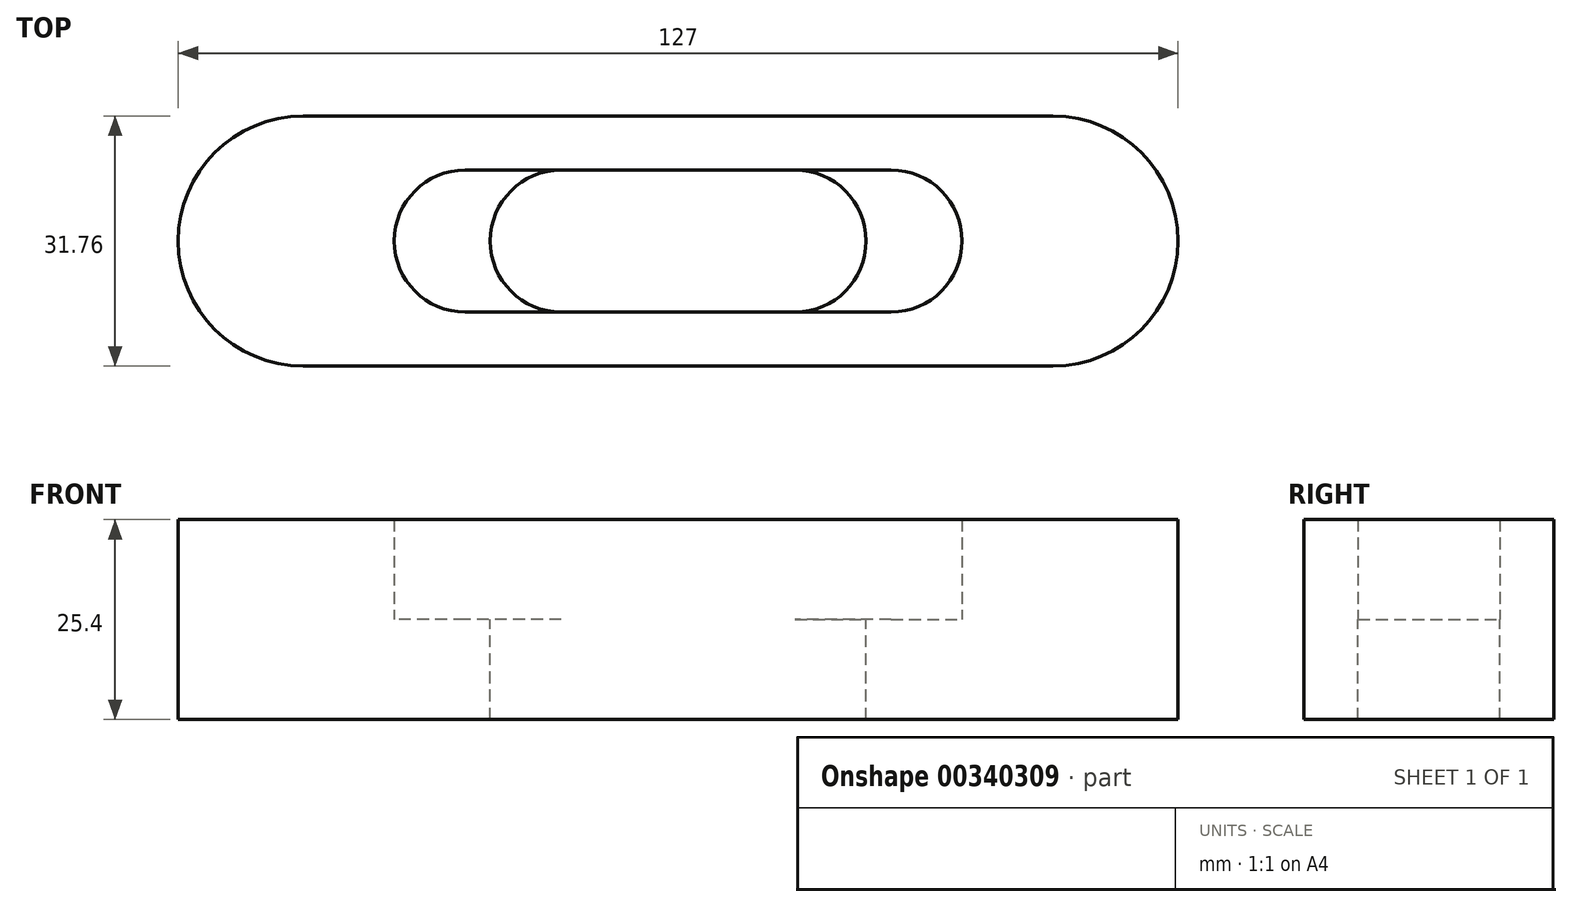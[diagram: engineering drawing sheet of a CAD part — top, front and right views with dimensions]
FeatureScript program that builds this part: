
annotation { "Feature Type Name" : "Feature", "Feature Type Description" : "" }
export const myFeature = defineFeature(function(context is Context, id is Id, definition is map)
    precondition{}
    {
        {
            var Q0;
            Q0=qCreatedBy(makeId("Top.planeOp"),FACE);
            var sketch = newSketch(context, id + "F0", { "sketchPlane" : qUnion([Q0])});
            skLineSegment(sketch, "E0.bottom", {"start": v(47.63, -15.88) * mm, "end": v(-47.63, -15.88) * mm});
            skLineSegment(sketch, "E0.top", {"start": v(47.63, 15.88) * mm, "end": v(-47.63, 15.87) * mm});
            skLineSegment(sketch, "E0.left", {"start": v(47.63, -15.88) * mm, "end": v(47.63, 15.88) * mm, "construction": true});
            skLineSegment(sketch, "E0.right", {"start": v(-47.63, -15.88) * mm, "end": v(-47.63, 15.88) * mm, "construction": true});
            skPoint(sketch, "E0.middle", {"position": v(0, 0) * mm});
            skLineSegment(sketch, "E1.bottom", {"start": v(27.05, -9.02) * mm, "end": v(-27.05, -9.02) * mm});
            skLineSegment(sketch, "E1.top", {"start": v(27.05, 9.02) * mm, "end": v(-27.05, 9.02) * mm});
            skLineSegment(sketch, "E1.left", {"start": v(27.05, -9.02) * mm, "end": v(27.05, 9.02) * mm, "construction": true});
            skLineSegment(sketch, "E1.right", {"start": v(-27.05, -9.02) * mm, "end": v(-27.05, 9.02) * mm, "construction": true});
            skArc(sketch, "E2", {"start": v(-47.62, 15.88) * mm, "mid": v(-63.5, 0) * mm, "end": v(-47.63, -15.88) * mm});
            skArc(sketch, "E3", {"start": v(47.63, -15.88) * mm, "mid": v(63.5, 0) * mm, "end": v(47.63, 15.88) * mm});
            skArc(sketch, "E4", {"start": v(27.05, -9.02) * mm, "mid": v(36.07, 0) * mm, "end": v(27.05, 9.02) * mm});
            skArc(sketch, "E5", {"start": v(-27.05, 9.02) * mm, "mid": v(-36.07, 0) * mm, "end": v(-27.05, -9.02) * mm});
            skSolve(sketch);
        }
        {
            var Q0;
            Q0 = qSketchRegion(id + "F0", true);
            extrude(context, id + "F1", {"entities" : qUnion([Q0]), "depth" : 12.7 * mm});
        }
        {
            var Q0;
            Q0=makeQuery(id+"F1.opExtrude","CAP_FACE",FACE,{"disambiguationData":[OSD([sQuery(id+"F0.wireOp",EDGE,"E0.bottom"),sQuery(id+"F0.wireOp",EDGE,"E0.top"),sQuery(id+"F0.wireOp",EDGE,"E1.bottom"),sQuery(id+"F0.wireOp",EDGE,"E1.top"),sQuery(id+"F0.wireOp",EDGE,"E2"),sQuery(id+"F0.wireOp",EDGE,"E3"),sQuery(id+"F0.wireOp",EDGE,"E4"),sQuery(id+"F0.wireOp",EDGE,"E5")])],"isStart":true});
            var sketch = newSketch(context, id + "F2", { "sketchPlane" : qUnion([Q0])});
            skLineSegment(sketch, "E6.bottom", {"start": v(14.86, -9.02) * mm, "end": v(-14.86, -9.02) * mm});
            skLineSegment(sketch, "E6.top", {"start": v(14.86, 9.02) * mm, "end": v(-14.86, 9.02) * mm});
            skLineSegment(sketch, "E6.left", {"start": v(14.86, -9.02) * mm, "end": v(14.86, 9.02) * mm});
            skLineSegment(sketch, "E6.right", {"start": v(-14.86, -9.02) * mm, "end": v(-14.86, 9.02) * mm});
            skPoint(sketch, "E6.middle", {"position": v(0, 0) * mm});
            skArc(sketch, "E7", {"start": v(14.86, -9.02) * mm, "mid": v(23.88, 0) * mm, "end": v(14.86, 9.02) * mm});
            skArc(sketch, "E8", {"start": v(-14.86, 9.02) * mm, "mid": v(-23.88, 0) * mm, "end": v(-14.86, -9.02) * mm});
            skSolve(sketch);
        }
        {
            var Q0;
            {var subQ6=sQuery(id+"F2.wireOp",EDGE,"E6.bottom");Q0=makeQuery(id+"F2.imprint","IMPRINT",FACE,{"disambiguationData":[TD([[makeQuery(id+"F2.imprint","IMPRINT",EDGE,{"derivedFrom":subQ6}),1.0]])]});}
            var Q1;
            {var subQ0=sQuery(id+"F2.wireOp",EDGE,"E8");Q1=makeQuery(id+"F2.imprint","IMPRINT",FACE,{"disambiguationData":[TD([[makeQuery(id+"F2.imprint","IMPRINT",EDGE,{"derivedFrom":subQ0}),-1.0]])]});}
            var Q2;
            {var subQ0=sQuery(id+"F2.wireOp",EDGE,"E7");Q2=makeQuery(id+"F2.imprint","IMPRINT",FACE,{"disambiguationData":[TD([[makeQuery(id+"F2.imprint","IMPRINT",EDGE,{"derivedFrom":subQ0}),-1.0]])]});}
            extrude(context, id + "F3", {"entities" : qUnion([Q0, Q1, Q2]), "operationType" : NewBodyOperationType.ADD, "depth" : 12.7 * mm});
        }
    });
